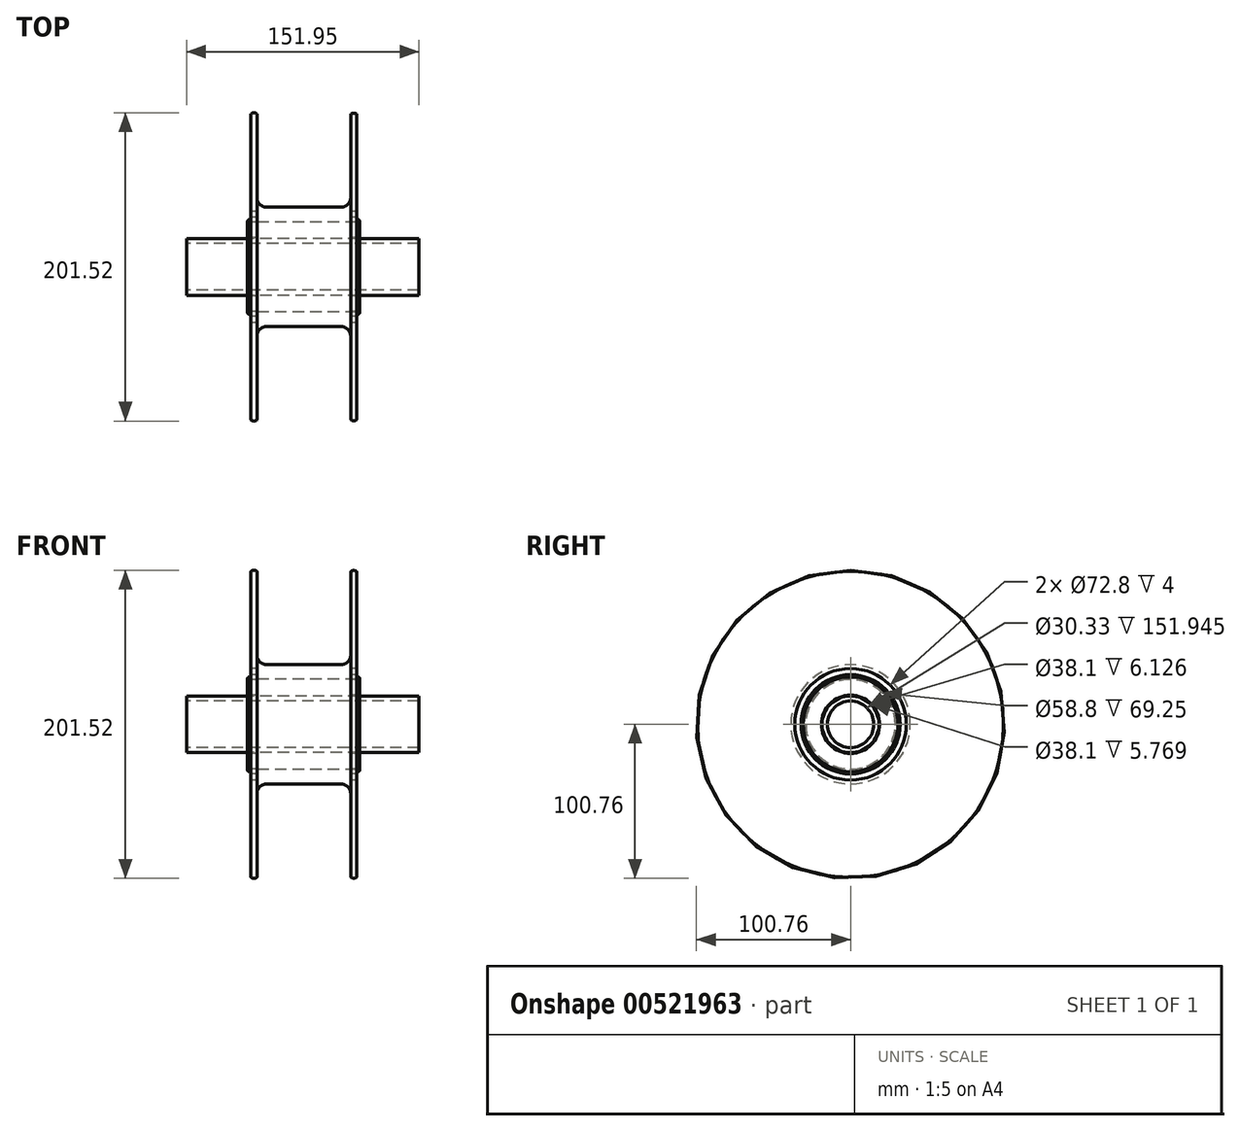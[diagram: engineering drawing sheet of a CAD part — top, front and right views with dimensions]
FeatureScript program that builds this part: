
annotation { "Feature Type Name" : "Feature", "Feature Type Description" : "" }
export const myFeature = defineFeature(function(context is Context, id is Id, definition is map)
    precondition{}
    {
        {
            var Q0;
            Q0=qCreatedBy(makeId("Front.planeOp"),FACE);
            var sketch = newSketch(context, id + "F0", { "sketchPlane" : qUnion([Q0])});
            skLineSegment(sketch, "E0", {"start": v(-72.08, 0) * mm, "end": v(73.42, 0) * mm, "construction": true});
            skLineSegment(sketch, "E1", {"start": v(-72.08, 100) * mm, "end": v(82.65, 100) * mm, "construction": true});
            skLineSegment(sketch, "E2", {"start": v(-74.18, 29.4) * mm, "end": v(74.17, 29.4) * mm, "construction": true});
            skLineSegment(sketch, "E3", {"start": v(0, 29.4) * mm, "end": v(-34.19, 29.4) * mm});
            skLineSegment(sketch, "E4", {"start": v(-34.19, 29.4) * mm, "end": v(-34.19, 32.4) * mm});
            skLineSegment(sketch, "E5", {"start": v(-30.19, 100) * mm, "end": v(-30.19, 45.35) * mm});
            skLineSegment(sketch, "E6", {"start": v(-23.84, 39) * mm, "end": v(24.71, 39) * mm});
            skLineSegment(sketch, "E7", {"start": v(31.06, 45.35) * mm, "end": v(31.06, 100) * mm});
            skLineSegment(sketch, "E8", {"start": v(35.06, 100) * mm, "end": v(35.06, 36.4) * mm});
            skLineSegment(sketch, "E9", {"start": v(35.06, 29.4) * mm, "end": v(0, 29.4) * mm});
            skArc(sketch, "E10", {"start": v(-30.19, 100) * mm, "mid": v(-32.19, 100.76) * mm, "end": v(-34.19, 100) * mm});
            skArc(sketch, "E11", {"start": v(35.06, 100) * mm, "mid": v(33.06, 100.54) * mm, "end": v(31.06, 100) * mm});
            skLineSegment(sketch, "E12.bottom", {"start": v(-34.19, 32.4) * mm, "end": v(-30.19, 32.4) * mm});
            skLineSegment(sketch, "E12.top", {"start": v(-34.19, 36.4) * mm, "end": v(-30.19, 36.4) * mm});
            skLineSegment(sketch, "E12.right", {"start": v(-30.19, 32.4) * mm, "end": v(-30.19, 36.4) * mm});
            skLineSegment(sketch, "E13.trimOffspring", {"start": v(-34.19, 36.4) * mm, "end": v(-34.19, 100) * mm});
            skLineSegment(sketch, "E14.bottom", {"start": v(35.06, 32.4) * mm, "end": v(31.06, 32.4) * mm});
            skLineSegment(sketch, "E14.top", {"start": v(35.06, 36.4) * mm, "end": v(31.06, 36.4) * mm});
            skLineSegment(sketch, "E14.right", {"start": v(31.06, 32.4) * mm, "end": v(31.06, 36.4) * mm});
            skLineSegment(sketch, "E15.trimOffspring", {"start": v(35.06, 32.4) * mm, "end": v(35.06, 29.4) * mm});
            skPoint(sketch, "E16.visualSharp", {"position": v(31.06, 39) * mm});
            skArc(sketch, "E16.filletArc", {"start": v(24.71, 39) * mm, "mid": v(29.2, 40.86) * mm, "end": v(31.06, 45.35) * mm});
            skPoint(sketch, "E17.visualSharp", {"position": v(-30.19, 39) * mm});
            skArc(sketch, "E17.filletArc", {"start": v(-30.19, 45.35) * mm, "mid": v(-28.33, 40.86) * mm, "end": v(-23.84, 39) * mm});
            skLineSegment(sketch, "E18", {"start": v(-30.2, 19.05) * mm, "end": v(-30.2, 29.23) * mm});
            skLineSegment(sketch, "E19", {"start": v(-30.2, 29.23) * mm, "end": v(-34.4, 29.23) * mm});
            skLineSegment(sketch, "E20", {"start": v(-34.4, 29.23) * mm, "end": v(-34.4, 30.9) * mm});
            skPoint(sketch, "E20.endSnap0", {"position": v(-34.19, 30.9) * mm});
            skLineSegment(sketch, "E21", {"start": v(-34.4, 30.9) * mm, "end": v(-36.32, 30.9) * mm});
            skLineSegment(sketch, "E22", {"start": v(-36.32, 30.9) * mm, "end": v(-36.32, 19.05) * mm});
            skLineSegment(sketch, "E23", {"start": v(-36.32, 19.05) * mm, "end": v(-30.2, 19.05) * mm});
            skLineSegment(sketch, "E24", {"start": v(31.1, 19.05) * mm, "end": v(31.1, 29.22) * mm});
            skLineSegment(sketch, "E25", {"start": v(31.1, 29.22) * mm, "end": v(35.23, 29.22) * mm});
            skLineSegment(sketch, "E26", {"start": v(35.23, 29.22) * mm, "end": v(35.23, 30.96) * mm});
            skLineSegment(sketch, "E27", {"start": v(35.23, 30.96) * mm, "end": v(36.86, 30.96) * mm});
            skLineSegment(sketch, "E28", {"start": v(36.86, 30.96) * mm, "end": v(36.86, 19.05) * mm});
            skLineSegment(sketch, "E29", {"start": v(36.86, 19.05) * mm, "end": v(31.1, 19.05) * mm});
            skLineSegment(sketch, "E30.bottom", {"start": v(-36.32, 19.05) * mm, "end": v(36.86, 19.05) * mm});
            skLineSegment(sketch, "E31.trimOffspring", {"start": v(-36.32, 19.05) * mm, "end": v(-30.2, 19.05) * mm, "construction": true});
            skLineSegment(sketch, "E32.trimOffspring", {"start": v(31.1, 19.05) * mm, "end": v(36.86, 19.05) * mm, "construction": true});
            skLineSegment(sketch, "E33", {"start": v(-79.79, 19.05) * mm, "end": v(80.4, 19.05) * mm, "construction": true});
            skLineSegment(sketch, "E34.bottom", {"start": v(-76.17, 15.17) * mm, "end": v(75.78, 15.17) * mm});
            skLineSegment(sketch, "E34.top", {"start": v(-76.17, 18.55) * mm, "end": v(75.78, 18.55) * mm});
            skLineSegment(sketch, "E34.left", {"start": v(-76.17, 15.17) * mm, "end": v(-76.17, 18.55) * mm});
            skLineSegment(sketch, "E34.right", {"start": v(75.78, 15.17) * mm, "end": v(75.78, 18.55) * mm});
            skSolve(sketch);
        }
        {
            var Q0;
            Q0=makeQuery(id+"F0.imprint","IMPRINT",FACE,{"disambiguationData":[TD([[makeQuery(id+"F0.imprint","IMPRINT",EDGE,{"derivedFrom":sQuery(id+"F0.wireOp",EDGE,"E3")}),-1.0]])]});
            var Q1;
            Q1=makeQuery(id+"F0.imprint","IMPRINT",FACE,{"disambiguationData":[TD([[makeQuery(id+"F0.imprint","IMPRINT",EDGE,{"derivedFrom":sQuery(id+"F0.wireOp",EDGE,"E18")}),1.0]])]});
            var Q2;
            Q2=makeQuery(id+"F0.imprint","IMPRINT",FACE,{"disambiguationData":[TD([[makeQuery(id+"F0.imprint","IMPRINT",EDGE,{"derivedFrom":sQuery(id+"F0.wireOp",EDGE,"E24")}),-1.0]])]});
            var Q3;
            Q3=makeQuery(id+"F0.imprint","IMPRINT",FACE,{"disambiguationData":[TD([[makeQuery(id+"F0.imprint","IMPRINT",EDGE,{"derivedFrom":sQuery(id+"F0.wireOp",EDGE,"E30.top")}),1.0]])]});
            var Q4;
            Q4=makeQuery(id+"F0.imprint","IMPRINT",FACE,{"disambiguationData":[TD([[makeQuery(id+"F0.imprint","IMPRINT",EDGE,{"derivedFrom":sQuery(id+"F0.wireOp",EDGE,"E34.bottom")}),1.0]])]});
            var Q5;
            Q5=sQuery(id+"F0.wireOp",EDGE,"E0");
            revolve(context, id + "F1", {"entities" : qUnion([Q0, Q1, Q2, Q3, Q4]), "axis" : qUnion([Q5]), "revolveType" : RevolveType.FULL});
        }
        {
            var Q0;
            Q0=makeQuery(id+"F1.opRevolve","SWEPT_EDGE",EDGE,{"disambiguationData":[OSD([sQuery(id+"F0.wireOp",EDGE,"E27"),sQuery(id+"F0.wireOp",EDGE,"E28")])]});
            var Q1;
            Q1=makeQuery(id+"F1.opRevolve","SWEPT_EDGE",EDGE,{"disambiguationData":[OSD([sQuery(id+"F0.wireOp",EDGE,"E21"),sQuery(id+"F0.wireOp",EDGE,"E22")])]});
            fillet(context, id + "F2", {"entities" : qUnion([Q0, Q1]), "radius" : 1 * mm, "tangentPropagation" : true, "allowEdgeOverflow" : false});
        }
    });
